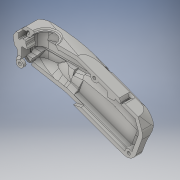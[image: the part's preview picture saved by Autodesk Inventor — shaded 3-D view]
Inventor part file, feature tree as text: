
AUTODESK INVENTOR PART (.ipt)
format: ipt  version: 2016 (Build 200138000, 138)  size: 2,501,120 bytes
history: native  units: in
note: dims shown in document units (in); Inventor stores cm internally (conversion verified against a paired STEP export)
features: extrude x63, sketch x54, fillet x37, projected_geometry x18, chamfer x17, other x11, direct_edit x9, move_body x9, plane x5, mirror x4, revolve x2, shell x1, split x1
ambient origin geometry x8: Origin, YZ Plane, XZ Plane, XY Plane, X Axis, Y Axis, Z Axis, Center Point
bodies: Solid1 (feature_tree)
feature tree (231):
  other  "base_geometry"
  extrude  "Extrusion1"  Depth=0.0748in
  other  "midplane"
  extrude  "Extrusion2"  Depth=0.4921in
  chamfer  "Chamfer2"  Distance=1.2992in
  mirror  "Mirror1"
  chamfer  "Chamfer3"  Distance=0.2362in
  fillet  "Fillet1"  Radius=0.4724in
  extrude  "Extrusion27"  Depth=0.7874in
  fillet  "Fillet18"  Radius=0.5906in
  fillet  "Fillet3"  Radius=0.5906in
  fillet  "Fillet4"  Radius=0.1575in
  chamfer  "Chamfer4"  Distance=0.1575in Angle=45.0deg
  fillet  "Fillet5"  Radius=0.9843in
  fillet  "Fillet6"  Radius=0.0394in
  fillet  "Fillet7"  Radius=0.1575in
  chamfer  "Chamfer5"  Distance=0.1575in
  extrude  "Extrusion3"  Depth=0.0787in
  chamfer  "Chamfer6"  Distance=0.0394in
  fillet  "Fillet10"  Radius=0.5in
  fillet  "Fillet12"  Radius=0.25in
  chamfer  "Chamfer10"  Distance=0.375in
  fillet  "Fillet19"  Radius=0.0625in
  fillet  "Fillet22"  Radius=0.2362in
  chamfer  "Chamfer11"  Distance=0.25in
  fillet  "Fillet23"  Radius=0.25in
  fillet  "Fillet24"  Radius=0.1575in
  shell  "Shell1"  Thickness=0.5709in
  split  "Split1"
  extrude  "Extrusion4"  Depth=0.0787in TaperAngle=0.0deg
  extrude  "Extrusion5"  Depth=0.0787in
  extrude  "Extrusion6"  Depth=0.0787in TaperAngle=0.0deg
  extrude  "Extrusion7"  Depth=0.0787in
  chamfer  "Chamfer7"  Distance=0.1575in
  plane  "Work Plane2"
  sketch  "Sketch9"  dims[d9=0.7874in]
  extrude  "Extrusion8"  Depth=0.0787in
  extrude  "Extrusion9"  Depth=0.0787in
  extrude  "Extrusion10"  Depth=0.0787in TaperAngle=0.0deg
  sketch  "Sketch11"  dims[d11=1.0994in]
  extrude  "Extrusion11"  Depth=0.0787in
  mirror  "Mirror2"
  extrude  "Extrusion12"  Depth=0.0787in
  extrude  "Extrusion13"  Depth=0.2756in
  extrude  "Extrusion14"  Depth=0.4331in
  extrude  "Extrusion15"  Depth=0.0787in TaperAngle=0.0deg
  extrude  "Extrusion16"  TaperAngle=180.0deg  [1 undecoded]
  extrude  "Extrusion17"  Depth=0.2362in
  extrude  "Extrusion18"  Depth=0.2362in
  extrude  "Extrusion19"  Depth=0.0787in TaperAngle=0.0deg
  extrude  "Extrusion20"  Depth=0.0787in
  extrude  "Extrusion21"  Depth=0.0394in TaperAngle=0.0deg
  extrude  "Extrusion22"  Depth=0.2362in
  extrude  "joystick_grip"  Depth=0.2362in
  extrude  "Extrusion24"  Depth=0.0787in TaperAngle=0.0deg
  extrude  "Extrusion25"  Depth=0.0787in
  plane  "Work Plane3"
  revolve  "Revolution3"  [1 undecoded]
  revolve  "Revolution4"  [1 undecoded]
  chamfer  "Chamfer9"  Distance=0.0591in
  extrude  "Extrusion29"  Depth=0.0787in
  fillet  "Fillet39"  Radius=0.0787in
  extrude  "Extrusion54"  Depth=0.0787in TaperAngle=0.0deg
  fillet  "Fillet40"  Radius=0.0394in
  direct_edit  "Direct Edit9"
  fillet  "Fillet41"  Radius=0.1969in
  chamfer  "Chamfer12"  Distance=0.2953in
  fillet  "Fillet27"  Radius=0.0394in
  extrude  "Extrusion30"  Depth=0.0787in
  fillet  "Fillet28"  Radius=0.2953in
  sketch  "Sketch36"  dims[d35=0.1378in]
  extrude  "Extrusion31"  Depth=0.0787in
  extrude  "Extrusion32"  Depth=0.0787in
  extrude  "Extrusion33"  Depth=0.0787in TaperAngle=0.0deg
  mirror  "Mirror3"
  fillet  "Fillet29"  Radius=0.1969in
  fillet  "Fillet30"  Radius=0.1575in
  fillet  "Fillet31"  Radius=0.1575in
  fillet  "Fillet32"  [1 undecoded]
  chamfer  "Chamfer13"  Distance=0.0787in
  chamfer  "Chamfer14"  Angle=90.0deg  [1 undecoded]
  extrude  "Extrusion34"  Depth=0.0394in TaperAngle=45.0deg
  fillet  "Fillet33"  Radius=0.5906in
  fillet  "Fillet34"  Radius=1.5748in
  sketch  "Sketch39"  dims[d39=0.1409in]
  extrude  "Extrusion35"  Depth=0.0787in
  extrude  "Extrusion36"  Depth=0.0787in
  extrude  "Extrusion37"  Depth=0.0787in
  sketch  "Sketch41"  dims[d41=0.2362in]
  extrude  "Extrusion38"  Depth=0.0787in TaperAngle=0.0deg
  extrude  "Extrusion39"  Depth=0.0787in
  extrude  "Extrusion40"  Depth=0.0787in
  extrude  "Extrusion41"  Depth=0.0787in
  extrude  "Extrusion42"  Depth=0.3937in
  chamfer  "Chamfer15"  Distance=0.2362in Angle=45.0deg
  extrude  "Extrusion43"  Depth=0.0787in
  plane  "Work Plane6"
  extrude  "Extrusion44"  Depth=0.0787in TaperAngle=45.0deg
  extrude  "Extrusion45"  Depth=0.0787in
  sketch  "Sketch47"  dims[d47=0.1575in]
  extrude  "Extrusion46"  Depth=0.2362in
  extrude  "Extrusion47"  Depth=0.0787in
  extrude  "Extrusion48"  Depth=0.0787in TaperAngle=0.0deg
  fillet  "Fillet35"  Radius=0.2756in
  sketch  "Sketch49"  dims[d49=1.0236in]
  extrude  "Extrusion49"  Depth=0.0787in
  direct_edit  "Direct Edit1"
  direct_edit  "Direct Edit2"
  fillet  "Fillet36"  Radius=1.0in
  chamfer  "Chamfer16"  Distance=0.2756in
  extrude  "Extrusion50"  Depth=0.0787in TaperAngle=0.0deg
  fillet  "Fillet37"  Radius=1.0in
  direct_edit  "Direct Edit3"
  direct_edit  "Direct Edit4"
  direct_edit  "Direct Edit5"
  extrude  "Extrusion51"  Depth=0.0787in TaperAngle=0.0deg
  mirror  "Mirror5"
  direct_edit  "Direct Edit6"
  direct_edit  "Direct Edit7"
  direct_edit  "Direct Edit8"
  fillet  "Fillet38"  Radius=0.2362in
  extrude  "Extrusion52"  Depth=0.0394in
  extrude  "Extrusion53"  Depth=0.0787in
  extrude  "Extrusion55"  Depth=0.0394in
  fillet  "Fillet42"  Radius=0.0591in
  extrude  "Extrusion56"  Depth=0.0787in TaperAngle=45.0deg
  fillet  "Fillet43"  Radius=0.0394in
  chamfer  "Chamfer19"  Distance=0.1181in
  fillet  "Fillet44"  Radius=1.0in
  extrude  "Extrusion57"  Depth=0.0787in
  fillet  "Fillet45"  Radius=0.1181in
  extrude  "Extrusion58"  Depth=0.0787in
  extrude  "Extrusion59"  Depth=0.0787in
  fillet  "Fillet46"  Radius=0.5945in
  fillet  "Fillet47"  [1 undecoded]
  extrude  "Extrusion60"  Depth=0.0787in
  chamfer  "Chamfer20"  Angle=30.0deg  [1 undecoded]
  fillet  "Fillet48"  Radius=0.1378in
  extrude  "Extrusion61"  TaperAngle=0.0deg  [1 undecoded]
  sketch  "Sketch60"  dims[d80=0.315in d81=0.125in d82=45.0deg d83=0.5906in d84=0.5906in d85=0.1575in d86=0.1575in d87=0.125in d88=45.0deg d89=0.9843in d90=0.0394in d91=0.0in]
  extrude  "Extrusion62"  TaperAngle=0.0deg  [1 undecoded]
  extrude  "Extrusion63"  Depth=0.0787in
  extrude  "Extrusion64"  Depth=0.0787in TaperAngle=0.0deg
  fillet  "Fillet49"  Radius=0.2953in
  extrude  "Extrusion65"  Depth=0.0787in
  chamfer  "Chamfer21"  Distance=0.3937in
  fillet  "Fillet50"  Radius=0.126in
  other  "Work Axis2"
  other  "Work Axis3"
  other  "Work Axis4"
  plane  "Work Plane4"
  sketch  "Sketch38"  dims[d38=1.2598in]
  plane  "Work Plane5"
  sketch  "Sketch2"  dims[d0=3.7402in d1=0.0748in]
  sketch  "Sketch3"  dims[d2=0.6299in d3=0.4921in]
  sketch  "Sketch4"  dims[d4=0.1969in]
  sketch  "Sketch5"  dims[d5=0.315in]
  sketch  "Sketch6"  dims[d6=0.4134in]
  sketch  "Sketch7"  dims[d7=90.0deg]
  sketch  "Sketch8"  dims[d8=45.0deg]
  sketch  "Sketch10"  dims[d10=0.315in]
  projected_geometry  "Projected Loop1"
  other  "pcb"
  sketch  "Sketch12"  dims[d12=2.5591in]
  sketch  "Sketch13"  dims[d13=1.2992in]
  projected_geometry  "Projected Loop2"
  sketch  "Sketch14"  dims[d14=0.6871in]
  projected_geometry  "Projected Loop3"
  sketch  "Sketch15"  dims[d15=0.5906in]
  sketch  "Sketch16"  dims[d16=0.8933in]
  projected_geometry  "Projected Loop4"
  sketch  "Sketch17"  dims[d17=0.1969in]
  sketch  "Sketch18"  dims[d19=2.9528in]
  projected_geometry  "Projected Loop5"
  sketch  "Sketch19"  dims[d20=0.1575in]
  projected_geometry  "Projected Loop6"
  sketch  "Sketch20"  dims[d21=0.1575in]
  sketch  "Sketch21"  dims[d22=0.2756in]
  projected_geometry  "Projected Loop7"
  sketch  "Sketch22"  dims[d23=0.1378in]
  other  "jstick_grip"
  sketch  "Sketch23"  dims[d28=0.5118in]
  projected_geometry  "Projected Loop8"
  sketch  "Sketch24"  dims[d29=0.1374in]
  sketch  "Sketch28"  dims[d31=1.9685in]
  projected_geometry  "Projected Loop9"
  sketch  "Sketch30"  dims[d32=0.2362in]
  projected_geometry  "Projected Loop10"
  projected_geometry  "Projected Loop11"
  sketch  "Sketch34"  dims[d33=0.1575in]
  other  "squeeze"
  sketch  "Sketch35"  dims[d34=0.1969in]
  other  "index"
  sketch  "Sketch37"  dims[d36=1.3189in]
  sketch  "Sketch40"  dims[d40=0.2126in]
  sketch  "Sketch42"  dims[d42=0.1575in]
  sketch  "Sketch43"  dims[d43=0.1378in]
  sketch  "Sketch44"  dims[d44=0.1969in]
  sketch  "Sketch45"  dims[d45=0.1772in]
  sketch  "Sketch46"  dims[d46=120.0deg]
  sketch  "Sketch48"  dims[d48=0.1575in]
  projected_geometry  "Projected Loop12"
  sketch  "Sketch50"  dims[d50=0.5906in]
  sketch  "Sketch51"  dims[d53=0.1614in]
  projected_geometry  "Projected Loop13"
  sketch  "Sketch52"  dims[d56=0.0618in]
  sketch  "Sketch53"  dims[d57=0.374in d59=1.2992in d60=0.0in]
  projected_geometry  "Projected Loop14"
  sketch  "Sketch54"  dims[d64=1.0in]
  sketch  "Sketch55"  dims[d65=45.0deg]
  sketch  "Sketch56"  dims[d66=1.1811in d68=0.2362in d69=0.0in]
  projected_geometry  "Projected Loop15"
  sketch  "Sketch57"  dims[d70=0.2362in d71=0.125in d72=45.0deg]
  sketch  "Sketch58"  dims[d73=0.2362in d74=0.125in d75=45.0deg d76=0.4724in]
  projected_geometry  "Projected Loop16"
  sketch  "Sketch59"  dims[d78=1.5748in d79=0.7874in]
  sketch  "Sketch61"  dims[d92=0.0394in d93=0.125in d94=45.0deg d97=0.1575in]
  sketch  "Sketch62"  dims[d99=0.5906in d101=0.1575in d102=0.126in d103=0.0394in d104=0.0in d105=0.5in d106=0.25in d107=0.0in d108=0.0in d109=0.25in d110=0.0in d111=0.375in d112=0.0in d113=0.0625in d114=0.125in d115=45.0deg d116=0.2362in d117=0.25in d118=0.0in d119=0.25in d120=0.0in d121=0.1575in d122=0.0in d123=0.5709in d124=0.0in d125=0.9646in d126=0.0in d127=0.6299in d130=0.4685in d131=0.0in d132=0.374in d133=0.1575in d134=0.1575in d135=0.374in d136=0.4685in d137=0.0in d138=0.315in d139=0.0591in d140=0.2756in d141=0.4331in d142=0.1969in d143=0.0in d144=180.0deg d145=0.2362in d146=0.2362in d147=0.1575in d148=0.0in d149=0.1378in d150=0.0394in d151=0.0in d152=0.2362in d153=0.2362in d154=0.1575in d155=0.0in d156=0.1378in d157=0.0394in d158=0.0in d159=0.1575in d160=0.0591in d161=0.0591in d162=0.0787in d163=0.2953in d164=0.0in d165=0.0394in d166=0.1969in d167=0.2953in d168=0.0in d169=0.0394in d170=0.1969in d171=0.2953in d172=0.0in d173=0.0039in d174=0.0787in d175=0.1969in d176=0.0in d177=0.1969in d178=0.0in d179=0.1575in d181=0.1575in d182=0.0in d194=90.0deg d196=0.0787in d199=90.0deg d200=0.0394in d201=0.125in d202=45.0deg d214=0.5906in d218=1.5748in d219=0.1969in d220=1.5748in d221=0.1969in d222=0.1575in d223=0.0in d224=0.1181in d225=15.748in d227=5.0in d229=0.3937in d234=0.2362in d235=0.125in d236=45.0deg d239=0.4724in d240=0.1575in d241=0.125in d242=45.0deg d243=0.4724in d244=0.2362in d247=0.1299in d248=1.0in d249=0.0in d250=0.2756in d251=0.125in d252=45.0deg d253=0.1969in d254=1.0in d255=0.0in d256=0.2756in d257=1.0in d258=0.0in d259=1.0in d260=0.0in d261=1.0in d262=0.0in d263=0.2362in d264=0.0394in d265=0.1575in d266=0.0394in d267=0.0591in d268=0.125in d269=45.0deg d270=0.1575in d271=0.125in d272=45.0deg d273=0.0394in d274=0.1181in d275=1.0in d276=0.0in d277=0.1969in d278=0.1181in d279=0.1787in d280=1.1811in d281=0.5945in d282=-2.1in d283=0.315in d284=30.0deg d285=0.1378in d286=0.0in d287=0.0in d288=0.0in d289=0.0in d290=0.3543in d291=0.0787in d292=0.0in d293=0.2953in d294=0.315in d295=0.3937in d296=0.126in d297=0.126in d298=0.315in d299=0.126in d300=0.0in d301=0.0in d302=0.0in d303=0.0in d304=0.0394in d305=0.0in d306=1.9488in d307=0.3543in d308=0.128in d309=0.0394in d310=0.0in d311=0.0492in d312=0.6693in d313=0.3937in d314=0.0in d315=0.0984in d316=0.125in d317=45.0deg d318=0.2362in d319=0.2362in d320=0.3937in d321=0.0in d322=-0.2362in d323=0.2362in d324=0.3937in d325=0.0in d326=0.3937in d327=0.0in d328=0.2362in d329=0.5512in d330=0.3937in d331=0.0in d332=0.3937in d333=0.0in d334=0.5118in d335=0.2362in d336=0.0394in d337=2.185in d338=0.2362in d339=0.3937in d340=0.0in d341=0.1969in d342=0.2244in d343=0.2244in d344=0.2244in d345=0.2244in d346=0.2646in d347=0.0in d348=0.0in d349=0.0in d350=-0.0197in d351=0.0in d352=0.0in d353=-0.0197in d354=0.1181in d355=0.0984in d356=0.125in d357=45.0deg d358=2.2638in d359=0.689in d360=0.0197in d361=0.0079in d362=0.3248in d363=0.3248in d364=0.0in d365=0.0in d366=0.1575in d367=0.0in d368=0.0in d369=-0.0197in d370=0.0in d371=0.0in d372=-0.0197in d373=-0.0295in d374=0.0in d375=0.0in d376=0.7874in d377=0.0138in d378=0.0in d379=0.0in d380=0.0197in d381=0.0in d382=0.0in d383=0.0in d384=-0.0197in d385=0.0in d386=0.0in d387=-0.0197in d388=0.0394in d389=0.4724in d390=0.0in d391=1.0138in d392=0.0in d393=0.1575in d394=0.6299in d395=0.0787in d396=0.0394in d397=0.7874in d399=0.0689in d400=0.7874in d402=0.0689in d405=1.0138in d406=0.0in d407=0.0787in d408=0.0in d409=0.0in d410=-0.0295in d411=0.0197in d412=0.0394in d413=3.1496in d415=0.0984in d416=0.3937in d418=1.0in d420=1.0138in d421=0.0in d428=0.1575in d429=0.315in d430=1.0138in d431=0.0in d432=0.1575in d433=0.1575in d434=0.125in d435=45.0deg d436=0.7874in d439=0.1614in d440=0.2362in d441=0.0in d442=0.0394in d443=0.2756in d444=0.0919in d445=0.2362in d446=0.0in d447=0.1181in d448=0.2362in d449=0.0in d450=0.2362in d451=0.0079in d452=1.5354in d453=1.8898in d455=0.2362in d456=0.0in d457=0.0394in d458=0.1181in d459=0.125in d460=45.0deg d461=0.315in d462=0.0984in d463=0.2362in d464=0.0in d465=0.0in d466=0.0in d467=0.0in d468=0.0in d469=60.0deg d470=0.2362in d471=0.0in d472=0.0197in d473=120.0deg d474=0.0787in d475=0.2362in d476=0.0in d477=0.0197in d478=0.125in d479=45.0deg d480=0.0787in]
  projected_geometry  "Projected Loop17"
  other  "right"
  other  "left"
  projected_geometry  "Project Cut Edges1"
  move_body  "Move1"
  move_body  "Move2"
  move_body  "Move3"
  move_body  "Move4"
  move_body  "Move5"
  move_body  "Move6"
  move_body  "Move7"
  move_body  "Move8"
  move_body  "Move9"
note: 9 required parameter values undecoded (feature->parameter linkage not recoverable at this tier; creation-order binding heuristic only, values carry confidence <= 0.55)